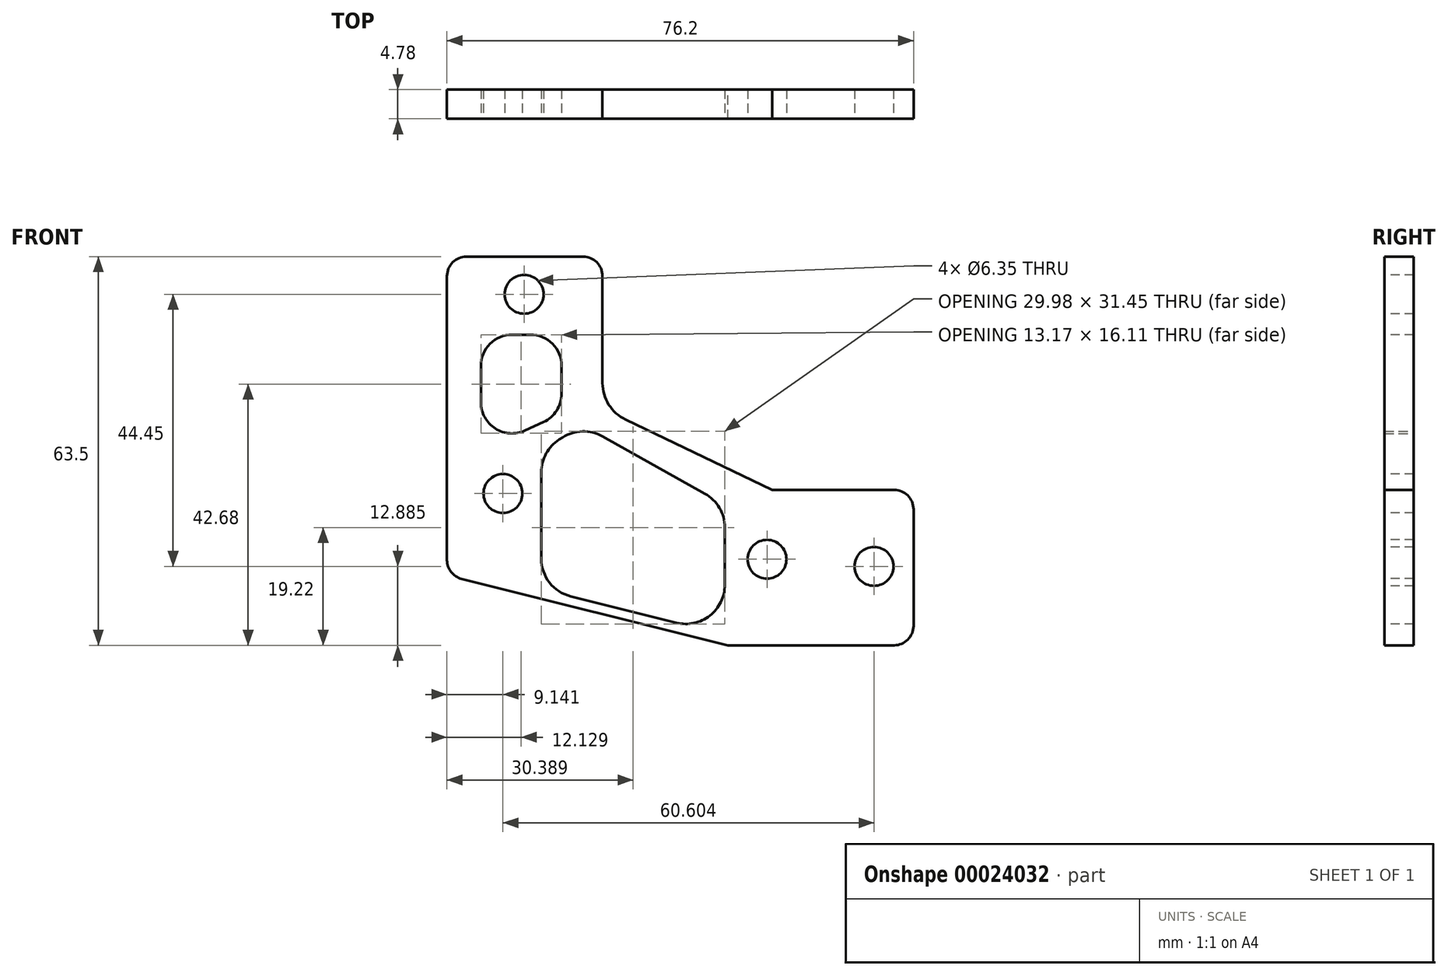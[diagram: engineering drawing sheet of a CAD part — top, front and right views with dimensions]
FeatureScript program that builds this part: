
annotation { "Feature Type Name" : "Feature", "Feature Type Description" : "" }
export const myFeature = defineFeature(function(context is Context, id is Id, definition is map)
    precondition{}
    {
        {
            var Q0;
            Q0=qCreatedBy(makeId("Front.planeOp"),FACE);
            var sketch = newSketch(context, id + "F0", { "sketchPlane" : qUnion([Q0])});
            skLineSegment(sketch, "E0.rect.bottom", {"start": v(-38.1, 31.75) * mm, "end": v(-12.7, 31.75) * mm});
            skLineSegment(sketch, "E0.rect.top", {"start": v(7.76, -31.75) * mm, "end": v(38.1, -31.75) * mm});
            skLineSegment(sketch, "E0.rect.left", {"start": v(-38.1, 31.75) * mm, "end": v(-38.1, -20.32) * mm});
            skLineSegment(sketch, "E0.rect.right", {"start": v(38.1, -6.35) * mm, "end": v(38.1, -31.75) * mm});
            skPoint(sketch, "E0.rect.middle", {"position": v(0, 0) * mm});
            skLineSegment(sketch, "E1", {"start": v(-38.1, -20.32) * mm, "end": v(7.76, -31.75) * mm});
            skLineSegment(sketch, "E2", {"start": v(38.1, -6.35) * mm, "end": v(15, -6.35) * mm});
            skLineSegment(sketch, "E3", {"start": v(15, -6.35) * mm, "end": v(-12.7, 6.92) * mm});
            skLineSegment(sketch, "E4", {"start": v(-12.7, 6.92) * mm, "end": v(-12.7, 31.75) * mm});
            skPoint(sketch, "E5", {"position": v(14.27, -17.88) * mm});
            skPoint(sketch, "E6", {"position": v(-25.4, 25.4) * mm});
            skPoint(sketch, "E7", {"position": v(-28.85, -7.14) * mm});
            skPoint(sketch, "E8", {"position": v(31.75, -19.05) * mm});
            skSolve(sketch);
        }
        {
            var Q0;
            Q0=makeQuery(id+"F0.imprint","IMPRINT",FACE,{"disambiguationData":[TD([[makeQuery(id+"F0.imprint","IMPRINT",EDGE,{"derivedFrom":sQuery(id+"F0.wireOp",EDGE,"E0.rect.bottom")}),-1.0]])]});
            extrude(context, id + "F1", {"entities" : qUnion([Q0]), "depth" : 4.78 * mm});
        }
        {
            var Q0;
            Q0=makeQuery(id+"F1.opExtrude","SWEPT_EDGE",EDGE,{"disambiguationData":[OSD([sQuery(id+"F0.wireOp",EDGE,"E3"),sQuery(id+"F0.wireOp",EDGE,"E4")])]});
            fillet(context, id + "F2", {"entities" : qUnion([Q0]), "radius" : 6.6 * mm, "tangentPropagation" : true, "allowEdgeOverflow" : false});
        }
        {
            var Q0;
            Q0=makeQuery(id+"F1.opExtrude","SWEPT_EDGE",EDGE,{"disambiguationData":[OSD([sQuery(id+"F0.wireOp",EDGE,"E0.rect.bottom"),sQuery(id+"F0.wireOp",EDGE,"E4")])]});
            var Q1;
            Q1=makeQuery(id+"F1.opExtrude","SWEPT_EDGE",EDGE,{"disambiguationData":[OSD([sQuery(id+"F0.wireOp",EDGE,"E0.rect.bottom"),sQuery(id+"F0.wireOp",EDGE,"E0.rect.left")])]});
            var Q2;
            Q2=makeQuery(id+"F1.opExtrude","SWEPT_EDGE",EDGE,{"disambiguationData":[OSD([sQuery(id+"F0.wireOp",EDGE,"E0.rect.left"),sQuery(id+"F0.wireOp",EDGE,"E1")])]});
            var Q3;
            Q3=makeQuery(id+"F1.opExtrude","SWEPT_EDGE",EDGE,{"disambiguationData":[OSD([sQuery(id+"F0.wireOp",EDGE,"E0.rect.right"),sQuery(id+"F0.wireOp",EDGE,"E2")])]});
            var Q4;
            Q4=makeQuery(id+"F1.opExtrude","SWEPT_EDGE",EDGE,{"disambiguationData":[OSD([sQuery(id+"F0.wireOp",EDGE,"E0.rect.top"),sQuery(id+"F0.wireOp",EDGE,"E0.rect.right")])]});
            fillet(context, id + "F3", {"entities" : qUnion([Q0, Q1, Q2, Q3, Q4]), "radius" : 3.17 * mm, "tangentPropagation" : true, "allowEdgeOverflow" : false});
        }
        {
            var Q0;
            Q0=makeQuery(id+"F1.opExtrude","CAP_FACE",FACE,{"disambiguationData":[OSD([sQuery(id+"F0.wireOp",EDGE,"E0.rect.bottom"),sQuery(id+"F0.wireOp",EDGE,"E0.rect.top"),sQuery(id+"F0.wireOp",EDGE,"E0.rect.left"),sQuery(id+"F0.wireOp",EDGE,"E0.rect.right"),sQuery(id+"F0.wireOp",EDGE,"E1"),sQuery(id+"F0.wireOp",EDGE,"E2"),sQuery(id+"F0.wireOp",EDGE,"E3"),sQuery(id+"F0.wireOp",EDGE,"E4")])],"isStart":false});
            var sketch = newSketch(context, id + "F4", { "sketchPlane" : qUnion([Q0])});
            skLineSegment(sketch, "E9.rect.bottom", {"start": v(-38.2, 31.93) * mm, "end": v(-12.8, 31.93) * mm});
            skLineSegment(sketch, "E9.rect.top", {"start": v(7.65, -31.57) * mm, "end": v(38, -31.57) * mm});
            skLineSegment(sketch, "E9.rect.left", {"start": v(-38.2, 31.93) * mm, "end": v(-38.2, -20.13) * mm});
            skLineSegment(sketch, "E9.rect.right", {"start": v(38, -6.17) * mm, "end": v(38, -31.57) * mm});
            skPoint(sketch, "E9.rect.middle", {"position": v(-0.1, 0.18) * mm});
            skLineSegment(sketch, "E10", {"start": v(-38.2, -20.13) * mm, "end": v(7.65, -31.57) * mm});
            skLineSegment(sketch, "E11", {"start": v(38, -6.17) * mm, "end": v(14.9, -6.17) * mm});
            skLineSegment(sketch, "E12", {"start": v(14.9, -6.17) * mm, "end": v(-12.8, 7.1) * mm});
            skLineSegment(sketch, "E13", {"start": v(-12.8, 7.1) * mm, "end": v(-12.8, 31.93) * mm});
            skPoint(sketch, "E14", {"position": v(14.17, -17.7) * mm});
            skPoint(sketch, "E15", {"position": v(-25.5, 25.58) * mm});
            skPoint(sketch, "E16", {"position": v(-28.96, -6.95) * mm});
            skPoint(sketch, "E17", {"position": v(31.65, -18.87) * mm});
            skSolve(sketch);
        }
        {
            var Q0;
            Q0=sQuery(id+"F4.wireOp",VERTEX,"E15");
            var Q1;
            Q1=sQuery(id+"F4.wireOp",VERTEX,"E16");
            var Q2;
            Q2=sQuery(id+"F4.wireOp",VERTEX,"E14");
            var Q3;
            Q3=sQuery(id+"F4.wireOp",VERTEX,"E17");
            var Q4;
            Q4=makeQuery(id+"F1.opExtrude","SWEPT_BODY",BODY,{"disambiguationData":[OSD([sQuery(id+"F0.wireOp",EDGE,"E0.rect.bottom"),sQuery(id+"F0.wireOp",EDGE,"E0.rect.top"),sQuery(id+"F0.wireOp",EDGE,"E0.rect.left"),sQuery(id+"F0.wireOp",EDGE,"E0.rect.right"),sQuery(id+"F0.wireOp",EDGE,"E1"),sQuery(id+"F0.wireOp",EDGE,"E2"),sQuery(id+"F0.wireOp",EDGE,"E3"),sQuery(id+"F0.wireOp",EDGE,"E4")])]});
            hole(context, id + "F5", {"style" : HoleStyle.SIMPLE, "holeDiameter" : 6.35 * mm, "endStyle" : HoleEndStyle.THROUGH, "locations" : qUnion([Q0, Q1, Q2, Q3]), "scope" : qUnion([Q4])});
        }
        {
            var Q0;
            Q0=makeQuery(id+"F1.opExtrude","CAP_FACE",FACE,{"disambiguationData":[OSD([sQuery(id+"F0.wireOp",EDGE,"E0.rect.bottom"),sQuery(id+"F0.wireOp",EDGE,"E0.rect.top"),sQuery(id+"F0.wireOp",EDGE,"E0.rect.left"),sQuery(id+"F0.wireOp",EDGE,"E0.rect.right"),sQuery(id+"F0.wireOp",EDGE,"E1"),sQuery(id+"F0.wireOp",EDGE,"E2"),sQuery(id+"F0.wireOp",EDGE,"E3"),sQuery(id+"F0.wireOp",EDGE,"E4")])],"isStart":false});
            var sketch = newSketch(context, id + "F6", { "sketchPlane" : qUnion([Q0])});
            skLineSegment(sketch, "E18", {"start": v(-32.56, 18.98) * mm, "end": v(-19.39, 18.98) * mm});
            skLineSegment(sketch, "E19", {"start": v(-19.39, 18.98) * mm, "end": v(-19.39, 6.09) * mm});
            skLineSegment(sketch, "E20", {"start": v(-19.39, 6.09) * mm, "end": v(-32.56, 0) * mm});
            skLineSegment(sketch, "E21", {"start": v(-32.56, 0) * mm, "end": v(-32.56, 18.98) * mm});
            skSolve(sketch);
        }
        {
            var Q0;
            Q0=makeQuery(id+"F6.imprint","IMPRINT",FACE,{"disambiguationData":[TD([[makeQuery(id+"F6.imprint","IMPRINT",EDGE,{"derivedFrom":sQuery(id+"F6.wireOp",EDGE,"E18")}),-1.0]])]});
            extrude(context, id + "F7", {"entities" : qUnion([Q0]), "operationType" : NewBodyOperationType.REMOVE, "oppositeDirection" : true, "depth" : 25.4 * mm});
        }
        {
            var Q0;
            Q0=makeQuery(id+"F7.boolean.opBoolean","COPY",EDGE,{"derivedFrom":makeQuery(id+"F7.opExtrude","SWEPT_EDGE",EDGE,{"disambiguationData":[OSD([sQuery(id+"F6.wireOp",EDGE,"E19"),sQuery(id+"F6.wireOp",EDGE,"E20")])]})});
            var Q1;
            Q1=makeQuery(id+"F7.boolean.opBoolean","COPY",EDGE,{"derivedFrom":makeQuery(id+"F7.opExtrude","SWEPT_EDGE",EDGE,{"disambiguationData":[OSD([sQuery(id+"F6.wireOp",EDGE,"E20"),sQuery(id+"F6.wireOp",EDGE,"E21")])]})});
            var Q2;
            Q2=makeQuery(id+"F7.boolean.opBoolean","COPY",EDGE,{"derivedFrom":makeQuery(id+"F7.opExtrude","SWEPT_EDGE",EDGE,{"disambiguationData":[OSD([sQuery(id+"F6.wireOp",EDGE,"E18"),sQuery(id+"F6.wireOp",EDGE,"E21")])]})});
            var Q3;
            Q3=makeQuery(id+"F7.boolean.opBoolean","COPY",EDGE,{"derivedFrom":makeQuery(id+"F7.opExtrude","SWEPT_EDGE",EDGE,{"disambiguationData":[OSD([sQuery(id+"F6.wireOp",EDGE,"E18"),sQuery(id+"F6.wireOp",EDGE,"E19")])]})});
            fillet(context, id + "F8", {"entities" : qUnion([Q0, Q1, Q2, Q3]), "radius" : 5.08 * mm, "tangentPropagation" : true, "allowEdgeOverflow" : false});
        }
        {
            var Q0;
            Q0=makeQuery(id+"F1.opExtrude","CAP_FACE",FACE,{"disambiguationData":[OSD([sQuery(id+"F0.wireOp",EDGE,"E0.rect.bottom"),sQuery(id+"F0.wireOp",EDGE,"E0.rect.top"),sQuery(id+"F0.wireOp",EDGE,"E0.rect.left"),sQuery(id+"F0.wireOp",EDGE,"E0.rect.right"),sQuery(id+"F0.wireOp",EDGE,"E1"),sQuery(id+"F0.wireOp",EDGE,"E2"),sQuery(id+"F0.wireOp",EDGE,"E3"),sQuery(id+"F0.wireOp",EDGE,"E4")])],"isStart":false});
            var sketch = newSketch(context, id + "F9", { "sketchPlane" : qUnion([Q0])});
            skLineSegment(sketch, "E22.rect.bottom", {"start": v(-38, 31.75) * mm, "end": v(-12.6, 31.75) * mm});
            skLineSegment(sketch, "E22.rect.top", {"start": v(7.8, -31.75) * mm, "end": v(38.2, -31.75) * mm});
            skLineSegment(sketch, "E22.rect.left", {"start": v(-38, 31.75) * mm, "end": v(-38, -20.33) * mm});
            skLineSegment(sketch, "E22.rect.right", {"start": v(38.2, -6.35) * mm, "end": v(38.2, -31.75) * mm});
            skPoint(sketch, "E22.rect.middle", {"position": v(0.1, 0) * mm});
            skLineSegment(sketch, "E23", {"start": v(-38, -20.33) * mm, "end": v(7.8, -31.75) * mm});
            skLineSegment(sketch, "E24", {"start": v(38.2, -6.35) * mm, "end": v(14.97, -6.35) * mm});
            skLineSegment(sketch, "E25", {"start": v(14.97, -6.35) * mm, "end": v(-12.6, 6.86) * mm});
            skLineSegment(sketch, "E26", {"start": v(-12.6, 6.86) * mm, "end": v(-12.6, 31.75) * mm});
            skPoint(sketch, "E27", {"position": v(14.38, -17.88) * mm});
            skPoint(sketch, "E28", {"position": v(-25.3, 25.4) * mm});
            skPoint(sketch, "E29", {"position": v(-28.75, -7.14) * mm});
            skPoint(sketch, "E30", {"position": v(31.85, -19.05) * mm});
            skLineSegment(sketch, "E31", {"start": v(-43.6, -17.35) * mm, "end": v(14.15, -31.75) * mm});
            skLineSegment(sketch, "E32", {"start": v(-22.7, -5.9) * mm, "end": v(-22.7, -22.56) * mm});
            skLineSegment(sketch, "E33", {"start": v(-22.7, -5.9) * mm, "end": v(-22.7, 0) * mm});
            skLineSegment(sketch, "E34", {"start": v(-22.7, 0) * mm, "end": v(-16.02, 4.24) * mm});
            skLineSegment(sketch, "E35", {"start": v(-16.02, 4.24) * mm, "end": v(7.28, -8.8) * mm});
            skLineSegment(sketch, "E36", {"start": v(7.28, -8.8) * mm, "end": v(7.28, -30.04) * mm});
            skSolve(sketch);
        }
        {
            var Q0;
            {var subQ1=sQuery(id+"F9.wireOp",EDGE,"E32");Q0=makeQuery(id+"F9.imprint","IMPRINT",FACE,{"disambiguationData":[TD([[makeQuery(id+"F9.imprint","IMPRINT",EDGE,{"derivedFrom":subQ1}),1.0]])]});}
            extrude(context, id + "F10", {"entities" : qUnion([Q0]), "operationType" : NewBodyOperationType.REMOVE, "oppositeDirection" : true, "depth" : 25.4 * mm});
        }
        {
            var Q0;
            Q0=makeQuery(id+"F10.boolean.opBoolean","COPY",EDGE,{"derivedFrom":makeQuery(id+"F10.opExtrude","SWEPT_EDGE",EDGE,{"disambiguationData":[OSD([sQuery(id+"F9.wireOp",EDGE,"E35"),sQuery(id+"F9.wireOp",EDGE,"E36")])]})});
            var Q1;
            Q1=makeQuery(id+"F10.boolean.opBoolean","COPY",EDGE,{"derivedFrom":makeQuery(id+"F10.opExtrude","SWEPT_EDGE",EDGE,{"disambiguationData":[OSD([sQuery(id+"F9.wireOp",EDGE,"E34"),sQuery(id+"F9.wireOp",EDGE,"E35")])]})});
            var Q2;
            Q2=makeQuery(id+"F10.boolean.opBoolean","COPY",EDGE,{"derivedFrom":makeQuery(id+"F10.opExtrude","SWEPT_EDGE",EDGE,{"disambiguationData":[OSD([sQuery(id+"F9.wireOp",EDGE,"E33"),sQuery(id+"F9.wireOp",EDGE,"E34")])]})});
            var Q3;
            Q3=makeQuery(id+"F10.boolean.opBoolean","COPY",EDGE,{"derivedFrom":makeQuery(id+"F10.opExtrude","SWEPT_EDGE",EDGE,{"disambiguationData":[OSD([sQuery(id+"F9.wireOp",EDGE,"E31"),sQuery(id+"F9.wireOp",EDGE,"E32")])]})});
            var Q4;
            Q4=makeQuery(id+"F10.boolean.opBoolean","COPY",EDGE,{"derivedFrom":makeQuery(id+"F10.opExtrude","SWEPT_EDGE",EDGE,{"disambiguationData":[OSD([sQuery(id+"F9.wireOp",EDGE,"E31"),sQuery(id+"F9.wireOp",EDGE,"E36")])]})});
            fillet(context, id + "F11", {"entities" : qUnion([Q0, Q1, Q2, Q3, Q4]), "radius" : 6.35 * mm, "tangentPropagation" : true, "allowEdgeOverflow" : false});
        }
    });
